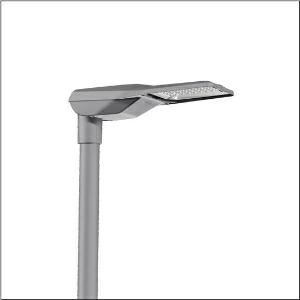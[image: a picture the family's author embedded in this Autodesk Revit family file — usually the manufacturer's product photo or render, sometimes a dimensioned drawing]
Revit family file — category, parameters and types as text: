
# Revit family: streetlight_sl_21_mini___pl52_5xe6h33a08hb_7bdf
name_source: partatom
category: Lighting Fixtures
units: mm (PartAtom-declared; Revit-internal decimal feet)

## family parameters
Cut with Voids When Loaded = No
Host = Face
Light Source = No
Part Type = Normal
Room Calculation Point = No
Round Connector Dimension = Use Diameter
Shared = No

## types (1)
- --- (1 x LED, 8890 lm, 66 W, 3000K)
    Apparent Load = 66 VA
    CIE Flux Codes = 27 59 98 100 100
    Color Rendering = 70
    Color Temperature = 3000K
    Default Elevation = 1800 mm
    Description = Streetlight SL 21 mini, mast luminaire, primary light control with lens, of PMMA, primary optical cover: cover, of toughened safety glass, transparent, light distribution: PL52, light emission: direct distribution, primary light characteristic: asymmetric, installation type: post-top, side-entry, LED, 3G 1.5mm², High Power LED, rated luminous flux: 8.890lm, luminous efficacy: 135lm/W, light colour: 730, colour temperature: 3000K, control: overheat protection, constant luminous flux control, time-dependent luminous flux control, flexible luminous flux parameterisation, mains connection: 230..240V, AC, 50/60Hz, connection cable pre-assembled, cable length: 8,5m, wiring characteristics: H07RN-F, start of lifetime: 66W, end of service life: 69W, reduction: 30W, luminaire housing, of diecast aluminium, powder-coated, Siteco® metallic grey (DB 702S), corrosivity category C5 mid according to DIN EN ISO 12944, please order mast flange separately, inclination adjustable: 0°, 5°, 10°, 15°, sealing non-destructively replaceable, multi-level sealing system, length: 628mm, width: 235mm, height: 110mm, mast flange for spigot size: 42mm (side-entry): 5XC10008XM4, 60/48mm (side-entry/post-top): 5XC10108XM2, 76/60mm (side-entry/post-top): 5XC10108XM1, protection rating (complete): IP66, insulation class (complete): insulation class II (safety insulation), certification: CE, ENEC, ENEC+, VDE, impact resistance: IK09, permissible operating ambient temperature for outdoor applications: -40..+50°C, standard-compliant lighting for roads and squares, packaging unit: 1 piece

Light Distribution: PL52
    Height = 110 mm
    Lamp = 1 x LED
    Lamp Light Flux = 8890 lm
    Lamp Power = 66 W
    Lamp count = 1
    Length = 625 mm
    Luminous efficacy = 135 lm/W
    Manufacturer = Siteco
    ModVariant = No
    Model = 5XE6H33A08HB
    Number of Poles = 1
    OnlyDefault = Yes
    Power Factor = 1
    Product Name = Streetlight SL 21 mini | PL52
    Product group = mast luminaire | pylon top
    ProductGroupID = 6100
    Protection Class = Protection class II
    Protection Degree = IP 66
    RLX_Detail_Level = 1
    RLX_Emergency_Light_Flux = 0 lm
    RLX_Emergency_Type = 0
    RLX_Emergency_Type_DB = No
    RlxData = <blob elided: 103569 chars, md5=a5bb07f7>
    Socket = socket
    Standby Power = 0 W
    System Light Flux = 8890 lm
    System Power = 66 W
    Type Comments = factory setting: luminous flux: 100 % | Output Level: 100 % | 670 mA
    Type Image = l_1003519.jpg
    URL = http://relux.com
    VarID = @adj_142161
    Voltage = 0 V
    Weight = 0.00 kg
    Width = 234 mm

## geometry (parser evidence)
native form markers: Blend x4, Sweep x9
no freeform markers — native parametric forms only
